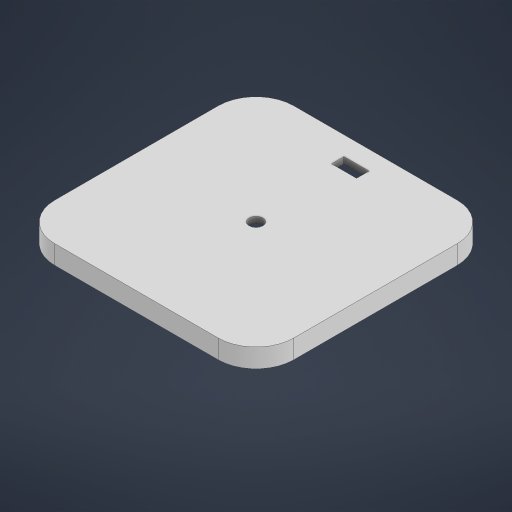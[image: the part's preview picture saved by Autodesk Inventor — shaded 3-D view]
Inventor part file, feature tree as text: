
AUTODESK INVENTOR PART (.ipt)
format: ipt  version: 2024 (Build 280153000, 153)  size: 399,872 bytes
history: native  units: mm
features: extrude x4, sketch x4, other x1, shell x1
ambient origin geometry x8: Origin, YZ Plane, XZ Plane, XY Plane, X Axis, Y Axis, Z Axis, Center Point
bodies: Body1 (feature_tree)
feature tree (10):
  other  "솔리드1"
  extrude  "돌출1"  Depth=190.0mm
  shell  "쉘1"  Thickness=190.0mm
  extrude  "돌출3"  Depth=30.0mm
  extrude  "돌출4"  Depth=15.0mm TaperAngle=0.0deg
  extrude  "돌출5"  Depth=5.0mm
  sketch  "스케치1"
  sketch  "스케치3"
  sketch  "스케치4"
  sketch  "스케치5"
